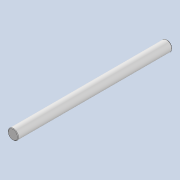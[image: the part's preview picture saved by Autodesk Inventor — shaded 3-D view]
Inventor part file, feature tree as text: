
AUTODESK INVENTOR PART (.ipt)
format: ipt  version: 2020 (Build 240168000, 168)  size: 78,336 bytes
history: native  units: mm
features: extrude x1, chamfer x1, sketch x1
ambient origin geometry x8: Origin, YZ Plane, XZ Plane, XY Plane, X Axis, Y Axis, Z Axis, Center Point
bodies: Solid1 (feature_tree)
feature tree (3):
  extrude  "Extrusion1"  Depth=150.0mm TaperAngle=0.0deg
  chamfer  "Chamfer1"  Distance=0.5mm Angle=45.0deg
  sketch  "Sketch1"  dims[d0=10.0mm d1=150.0mm d2=0.0mm d3=0.5mm d4=2.0mm d5=45.0deg]
